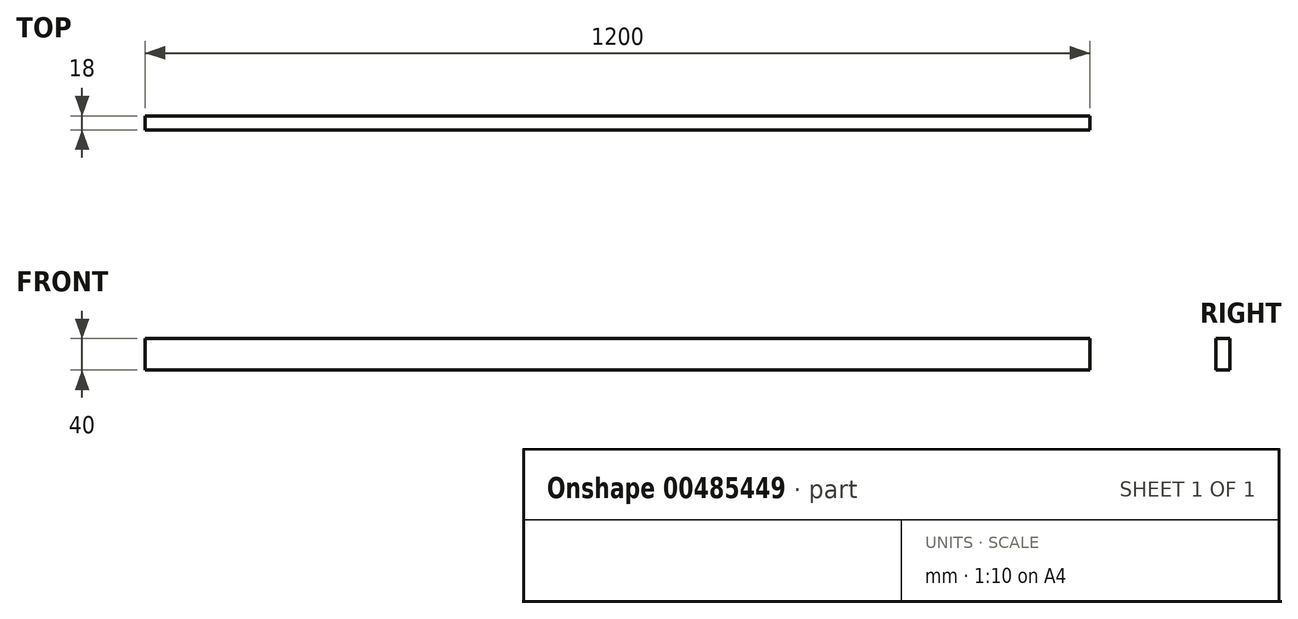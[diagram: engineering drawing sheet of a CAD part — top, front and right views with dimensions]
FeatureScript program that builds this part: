
annotation { "Feature Type Name" : "Feature", "Feature Type Description" : "" }
export const myFeature = defineFeature(function(context is Context, id is Id, definition is map)
    precondition{}
    {
        {
            var Q0;
            Q0=qCreatedBy(makeId("Front.planeOp"),FACE);
            var sketch = newSketch(context, id + "F0", { "sketchPlane" : qUnion([Q0])});
            skLineSegment(sketch, "E0.bottom", {"start": v(-600, 0) * mm, "end": v(600, 0) * mm});
            skLineSegment(sketch, "E0.top", {"start": v(-600, 40) * mm, "end": v(600, 40) * mm});
            skLineSegment(sketch, "E0.left", {"start": v(-600, 0) * mm, "end": v(-600, 40) * mm});
            skLineSegment(sketch, "E0.right", {"start": v(600, 0) * mm, "end": v(600, 40) * mm});
            skSolve(sketch);
        }
        {
            var Q0;
            Q0 = qSketchRegion(id + "F0", true);
            extrude(context, id + "F1", {"entities" : qUnion([Q0]), "depth" : 18 * mm});
        }
    });
